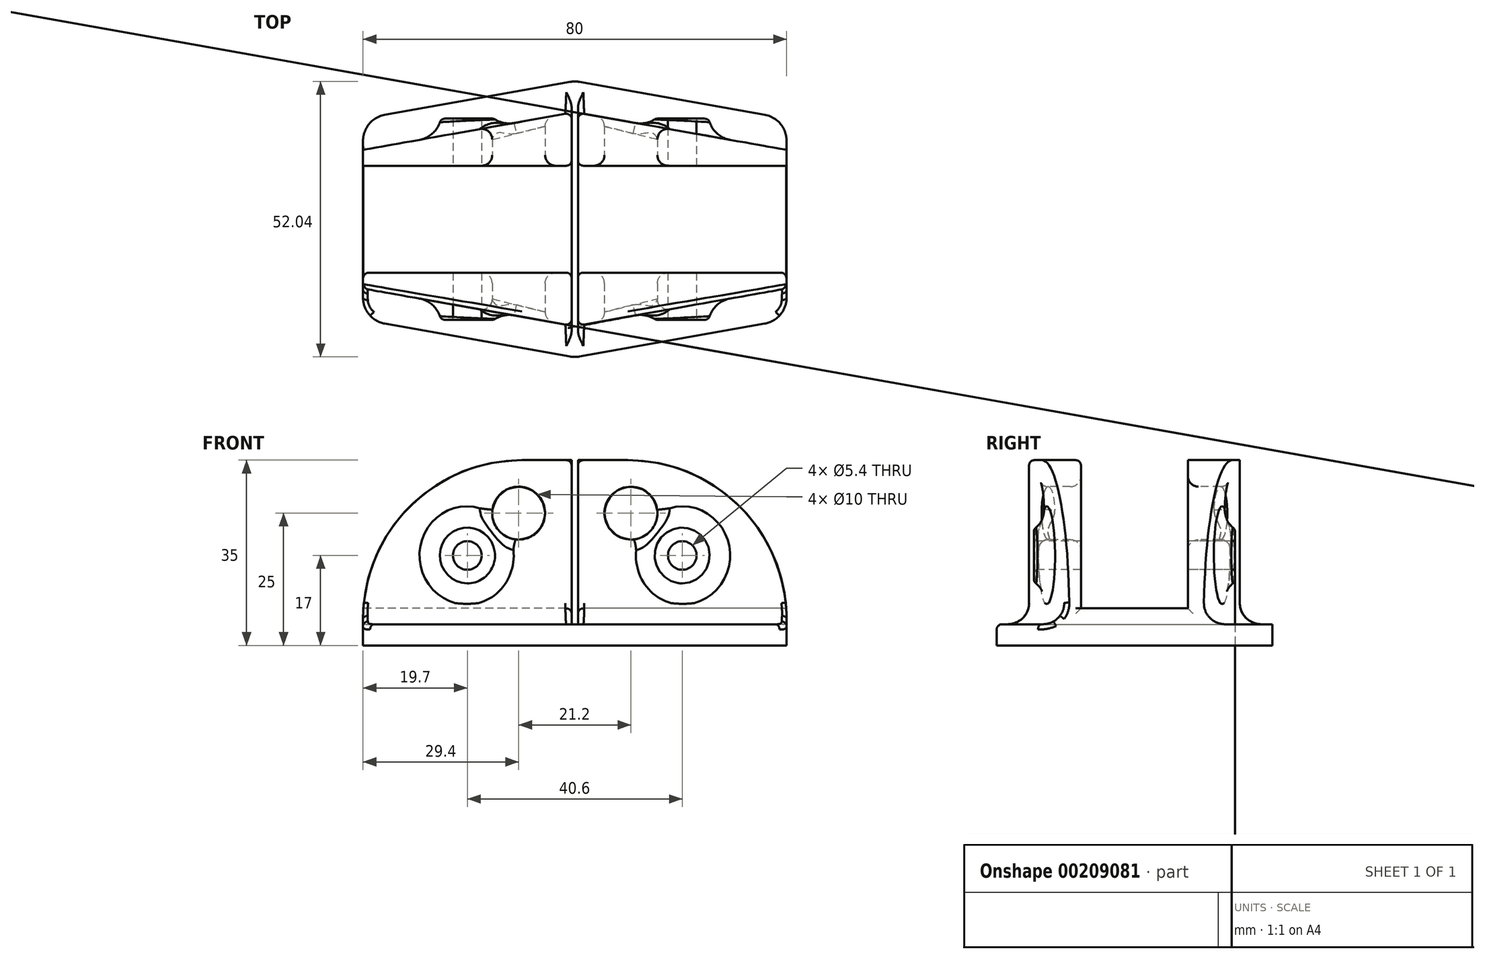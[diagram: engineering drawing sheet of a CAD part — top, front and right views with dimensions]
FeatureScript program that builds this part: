
annotation { "Feature Type Name" : "Feature", "Feature Type Description" : "" }
export const myFeature = defineFeature(function(context is Context, id is Id, definition is map)
    precondition{}
    {
        {
            var Q0;
            Q0=qCreatedBy(makeId("Top.planeOp"),FACE);
            var sketch = newSketch(context, id + "F0", { "sketchPlane" : qUnion([Q0])});
            skLineSegment(sketch, "E0.rect.bottom", {"start": v(40, 10.1) * mm, "end": v(-40, 10.1) * mm});
            skLineSegment(sketch, "E0.rect.top", {"start": v(40, -10.1) * mm, "end": v(-40, -10.1) * mm});
            skLineSegment(sketch, "E0.rect.left", {"start": v(40, 10.1) * mm, "end": v(40, -10.1) * mm});
            skLineSegment(sketch, "E0.rect.right", {"start": v(-40, 10.1) * mm, "end": v(-40, -10.1) * mm});
            skPoint(sketch, "E0.rect.middle", {"position": v(0, 0) * mm});
            skLineSegment(sketch, "E1", {"start": v(-40, 20.1) * mm, "end": v(40, 20.1) * mm, "construction": true});
            skLineSegment(sketch, "E2", {"start": v(40, -20.1) * mm, "end": v(-40, -20.1) * mm, "construction": true});
            skLineSegment(sketch, "E3", {"start": v(40, 10.1) * mm, "end": v(40, 20.1) * mm});
            skLineSegment(sketch, "E4", {"start": v(40, -10.1) * mm, "end": v(40, -20.1) * mm});
            skLineSegment(sketch, "E5.rect.bottom", {"start": v(0.6, 20.1) * mm, "end": v(-0.6, 20.1) * mm});
            skLineSegment(sketch, "E5.rect.top", {"start": v(0.6, -20.1) * mm, "end": v(-0.6, -20.1) * mm});
            skLineSegment(sketch, "E5.rect.left", {"start": v(0.6, 20.1) * mm, "end": v(0.6, 10.1) * mm});
            skLineSegment(sketch, "E5.rect.right", {"start": v(-0.6, 20.1) * mm, "end": v(-0.6, 10.1) * mm});
            skLineSegment(sketch, "E6", {"start": v(-40, -10.1) * mm, "end": v(-40, -20.1) * mm});
            skLineSegment(sketch, "E7", {"start": v(-40, 10.1) * mm, "end": v(-40, 20.1) * mm});
            skLineSegment(sketch, "E8.trimOffspring", {"start": v(0.6, -10.1) * mm, "end": v(0.6, -20.1) * mm});
            skLineSegment(sketch, "E9.trimOffspring", {"start": v(-0.6, -10.1) * mm, "end": v(-0.6, -20.1) * mm});
            skLineSegment(sketch, "E10", {"start": v(-40, 26.1) * mm, "end": v(40, 26.1) * mm, "construction": true});
            skLineSegment(sketch, "E11", {"start": v(40, -26.1) * mm, "end": v(-40, -26.1) * mm, "construction": true});
            skLineSegment(sketch, "E12", {"start": v(40, -20.1) * mm, "end": v(40, -26.1) * mm});
            skLineSegment(sketch, "E13", {"start": v(-40, -26.1) * mm, "end": v(-40, -20.1) * mm});
            skLineSegment(sketch, "E14", {"start": v(-40, 20.1) * mm, "end": v(-40, 26.1) * mm});
            skLineSegment(sketch, "E15", {"start": v(40, 26.1) * mm, "end": v(40, 20.1) * mm});
            skLineSegment(sketch, "E16", {"start": v(0.6, 10.1) * mm, "end": v(0.6, -10.1) * mm});
            skLineSegment(sketch, "E17", {"start": v(-0.6, -10.1) * mm, "end": v(-0.6, 10.1) * mm});
            skLineSegment(sketch, "E18", {"start": v(0.6, 20.1) * mm, "end": v(40, 13.1) * mm});
            skLineSegment(sketch, "E19", {"start": v(-0.6, 20.1) * mm, "end": v(-40, 13.1) * mm});
            skLineSegment(sketch, "E20", {"start": v(40, -13.1) * mm, "end": v(0.6, -20.1) * mm});
            skLineSegment(sketch, "E21", {"start": v(-0.6, -20.1) * mm, "end": v(-40, -13.1) * mm});
            skLineSegment(sketch, "E22", {"start": v(0, 26.1) * mm, "end": v(40, 19) * mm});
            skLineSegment(sketch, "E23", {"start": v(0, 26.1) * mm, "end": v(-40, 19) * mm});
            skLineSegment(sketch, "E24", {"start": v(0, -26.1) * mm, "end": v(40, -19) * mm});
            skLineSegment(sketch, "E25", {"start": v(0, -26.1) * mm, "end": v(-40, -19) * mm});
            skSolve(sketch);
        }
        {
            var Q0;
            Q0=makeQuery(id+"F0.imprint","IMPRINT",FACE,{"disambiguationData":[TD([[makeQuery(id+"F0.imprint","IMPRINT",EDGE,{"derivedFrom":sQuery(id+"F0.wireOp",EDGE,"E5.rect.bottom")}),-1.0]])]});
            var Q1;
            {var subQ4=sQuery(id+"F0.wireOp",EDGE,"E5.rect.right");Q1=makeQuery(id+"F0.imprint","IMPRINT",FACE,{"disambiguationData":[TD([[makeQuery(id+"F0.imprint","IMPRINT",EDGE,{"derivedFrom":subQ4}),-1.0]])]});}
            var Q2;
            Q2=makeQuery(id+"F0.imprint","IMPRINT",FACE,{"disambiguationData":[TD([[makeQuery(id+"F0.imprint","IMPRINT",EDGE,{"derivedFrom":sQuery(id+"F0.wireOp",EDGE,"E5.rect.bottom")}),1.0]])]});
            var Q3;
            {var subQ1=sQuery(id+"F0.wireOp",EDGE,"E5.rect.left");Q3=makeQuery(id+"F0.imprint","IMPRINT",FACE,{"disambiguationData":[TD([[makeQuery(id+"F0.imprint","IMPRINT",EDGE,{"derivedFrom":subQ1}),1.0]])]});}
            var Q4;
            {var subQ1=sQuery(id+"F0.wireOp",EDGE,"E0.rect.left");Q4=makeQuery(id+"F0.imprint","IMPRINT",FACE,{"disambiguationData":[TD([[makeQuery(id+"F0.imprint","IMPRINT",EDGE,{"derivedFrom":subQ1}),-1.0]])]});}
            var Q5;
            Q5=makeQuery(id+"F0.imprint","IMPRINT",FACE,{"disambiguationData":[TD([[makeQuery(id+"F0.imprint","IMPRINT",EDGE,{"derivedFrom":sQuery(id+"F0.wireOp",EDGE,"E5.rect.top")}),-1.0]])]});
            var Q6;
            {var subQ1=sQuery(id+"F0.wireOp",EDGE,"E9.trimOffspring");Q6=makeQuery(id+"F0.imprint","IMPRINT",FACE,{"disambiguationData":[TD([[makeQuery(id+"F0.imprint","IMPRINT",EDGE,{"derivedFrom":subQ1}),-1.0]])]});}
            var Q7;
            {var subQ1=sQuery(id+"F0.wireOp",EDGE,"E8.trimOffspring");Q7=makeQuery(id+"F0.imprint","IMPRINT",FACE,{"disambiguationData":[TD([[makeQuery(id+"F0.imprint","IMPRINT",EDGE,{"derivedFrom":subQ1}),1.0]])]});}
            var Q8;
            Q8=makeQuery(id+"F0.imprint","IMPRINT",FACE,{"disambiguationData":[TD([[makeQuery(id+"F0.imprint","IMPRINT",EDGE,{"derivedFrom":sQuery(id+"F0.wireOp",EDGE,"E5.rect.top")}),1.0]])]});
            var Q9;
            {var subQ1=sQuery(id+"F0.wireOp",EDGE,"E16");Q9=makeQuery(id+"F0.imprint","IMPRINT",FACE,{"disambiguationData":[TD([[makeQuery(id+"F0.imprint","IMPRINT",EDGE,{"derivedFrom":subQ1}),-1.0]])]});}
            var Q10;
            {var subQ1=sQuery(id+"F0.wireOp",EDGE,"E0.rect.right");Q10=makeQuery(id+"F0.imprint","IMPRINT",FACE,{"disambiguationData":[TD([[makeQuery(id+"F0.imprint","IMPRINT",EDGE,{"derivedFrom":subQ1}),1.0]])]});}
            extrude(context, id + "F1", {"entities" : qUnion([Q0, Q1, Q2, Q3, Q4, Q5, Q6, Q7, Q8, Q9, Q10]), "depth" : 4 * mm});
        }
        {
            var Q0;
            {var subQ1=sQuery(id+"F0.wireOp",EDGE,"E9.trimOffspring");Q0=makeQuery(id+"F0.imprint","IMPRINT",FACE,{"disambiguationData":[TD([[makeQuery(id+"F0.imprint","IMPRINT",EDGE,{"derivedFrom":subQ1}),-1.0]])]});}
            var Q1;
            {var subQ1=sQuery(id+"F0.wireOp",EDGE,"E8.trimOffspring");Q1=makeQuery(id+"F0.imprint","IMPRINT",FACE,{"disambiguationData":[TD([[makeQuery(id+"F0.imprint","IMPRINT",EDGE,{"derivedFrom":subQ1}),1.0]])]});}
            var Q2;
            {var subQ1=sQuery(id+"F0.wireOp",EDGE,"E5.rect.left");Q2=makeQuery(id+"F0.imprint","IMPRINT",FACE,{"disambiguationData":[TD([[makeQuery(id+"F0.imprint","IMPRINT",EDGE,{"derivedFrom":subQ1}),1.0]])]});}
            var Q3;
            {var subQ4=sQuery(id+"F0.wireOp",EDGE,"E5.rect.right");Q3=makeQuery(id+"F0.imprint","IMPRINT",FACE,{"disambiguationData":[TD([[makeQuery(id+"F0.imprint","IMPRINT",EDGE,{"derivedFrom":subQ4}),-1.0]])]});}
            extrude(context, id + "F2", {"entities" : qUnion([Q0, Q1, Q2, Q3]), "operationType" : NewBodyOperationType.ADD, "depth" : 35 * mm});
        }
        {
            var Q0;
            {var subQ1=sQuery(id+"F0.wireOp",EDGE,"E0.rect.right");Q0=makeQuery(id+"F0.imprint","IMPRINT",FACE,{"disambiguationData":[TD([[makeQuery(id+"F0.imprint","IMPRINT",EDGE,{"derivedFrom":subQ1}),1.0]])]});}
            var Q1;
            {var subQ1=sQuery(id+"F0.wireOp",EDGE,"E0.rect.left");Q1=makeQuery(id+"F0.imprint","IMPRINT",FACE,{"disambiguationData":[TD([[makeQuery(id+"F0.imprint","IMPRINT",EDGE,{"derivedFrom":subQ1}),-1.0]])]});}
            extrude(context, id + "F3", {"entities" : qUnion([Q0, Q1]), "operationType" : NewBodyOperationType.ADD, "depth" : 7 * mm});
        }
        {
            var Q0;
            Q0=qCreatedBy(makeId("Front.planeOp"),FACE);
            var sketch = newSketch(context, id + "F4", { "sketchPlane" : qUnion([Q0])});
            skLineSegment(sketch, "E26.0", {"start": v(-0.6, 7) * mm, "end": v(-40, 7) * mm});
            skLineSegment(sketch, "E27.0", {"start": v(40, 7) * mm, "end": v(0.6, 7) * mm});
            skLineSegment(sketch, "E28", {"start": v(-20.3, 7) * mm, "end": v(-20.3, 17) * mm, "construction": true});
            skLineSegment(sketch, "E29", {"start": v(20.3, 7) * mm, "end": v(20.3, 17) * mm, "construction": true});
            skCircle(sketch, "E30", {"center": v(-20.3, 17) * mm, "radius": 2.7 * mm});
            skCircle(sketch, "E31", {"center": v(20.3, 17) * mm, "radius": 2.7 * mm});
            skCircle(sketch, "E32", {"center": v(-20.3, 17) * mm, "radius": 5 * mm});
            skCircle(sketch, "E33", {"center": v(20.3, 17) * mm, "radius": 5 * mm});
            skCircle(sketch, "E34", {"center": v(-10.6, 25) * mm, "radius": 5 * mm});
            skCircle(sketch, "E35", {"center": v(10.6, 25) * mm, "radius": 5 * mm});
            skLineSegment(sketch, "E36.0", {"start": v(-0.6, 35) * mm, "end": v(-0.6, 7) * mm});
            skLineSegment(sketch, "E37.0", {"start": v(0.6, 35) * mm, "end": v(0.6, 7) * mm});
            skLineSegment(sketch, "E38", {"start": v(-10.6, 25) * mm, "end": v(-0.6, 25) * mm, "construction": true});
            skLineSegment(sketch, "E39", {"start": v(10.6, 25) * mm, "end": v(0.6, 25) * mm, "construction": true});
            skSolve(sketch);
        }
        {
            var Q0;
            Q0=makeQuery(id+"F4.imprint","IMPRINT",FACE,{"disambiguationData":[TD([[makeQuery(id+"F4.imprint","IMPRINT",EDGE,{"derivedFrom":sQuery(id+"F4.wireOp",EDGE,"E30")}),1.0]])]});
            var Q1;
            Q1=makeQuery(id+"F4.imprint","IMPRINT",FACE,{"disambiguationData":[TD([[makeQuery(id+"F4.imprint","IMPRINT",EDGE,{"derivedFrom":sQuery(id+"F4.wireOp",EDGE,"E31")}),1.0]])]});
            extrude(context, id + "F5", {"entities" : qUnion([Q0, Q1]), "operationType" : NewBodyOperationType.REMOVE, "endBound" : BoundingType.SYMMETRIC, "oppositeDirection" : true, "depth" : 50 * mm});
        }
        {
            var Q0;
            Q0=makeQuery(id+"F4.imprint","IMPRINT",FACE,{"disambiguationData":[TD([[makeQuery(id+"F4.imprint","IMPRINT",EDGE,{"derivedFrom":sQuery(id+"F4.wireOp",EDGE,"E30")}),-1.0]])]});
            var Q1;
            Q1=makeQuery(id+"F4.imprint","IMPRINT",FACE,{"disambiguationData":[TD([[makeQuery(id+"F4.imprint","IMPRINT",EDGE,{"derivedFrom":sQuery(id+"F4.wireOp",EDGE,"E31")}),-1.0]])]});
            extrude(context, id + "F6", {"entities" : qUnion([Q0, Q1]), "operationType" : NewBodyOperationType.ADD, "endBound" : BoundingType.SYMMETRIC, "depth" : 38 * mm});
        }
        {
            var Q0;
            Q0=makeQuery(id+"F4.imprint","IMPRINT",FACE,{"disambiguationData":[TD([[makeQuery(id+"F4.imprint","IMPRINT",EDGE,{"derivedFrom":sQuery(id+"F4.wireOp",EDGE,"E30")}),-1.0]])]});
            var Q1;
            Q1=makeQuery(id+"F4.imprint","IMPRINT",FACE,{"disambiguationData":[TD([[makeQuery(id+"F4.imprint","IMPRINT",EDGE,{"derivedFrom":sQuery(id+"F4.wireOp",EDGE,"E31")}),-1.0]])]});
            extrude(context, id + "F7", {"entities" : qUnion([Q0, Q1]), "operationType" : NewBodyOperationType.REMOVE, "endBound" : BoundingType.SYMMETRIC, "oppositeDirection" : true, "depth" : 20.2 * mm});
        }
        {
            var Q0;
            Q0=makeQuery(id+"F4.imprint","IMPRINT",FACE,{"disambiguationData":[TD([[makeQuery(id+"F4.imprint","IMPRINT",EDGE,{"derivedFrom":sQuery(id+"F4.wireOp",EDGE,"E34")}),1.0]])]});
            var Q1;
            Q1=makeQuery(id+"F4.imprint","IMPRINT",FACE,{"disambiguationData":[TD([[makeQuery(id+"F4.imprint","IMPRINT",EDGE,{"derivedFrom":sQuery(id+"F4.wireOp",EDGE,"E35")}),1.0]])]});
            extrude(context, id + "F8", {"entities" : qUnion([Q0, Q1]), "operationType" : NewBodyOperationType.REMOVE, "endBound" : BoundingType.SYMMETRIC, "oppositeDirection" : true, "depth" : 50 * mm});
        }
        {
            var Q0;
            Q0=makeQuery(id+"F2.opExtrude","CAP_EDGE",EDGE,{"disambiguationData":[OSD([sQuery(id+"F0.wireOp",EDGE,"E4")])],"isStart":false});
            var Q1;
            Q1=makeQuery(id+"F2.opExtrude","CAP_EDGE",EDGE,{"disambiguationData":[OSD([sQuery(id+"F0.wireOp",EDGE,"E6")])],"isStart":false});
            var Q2;
            Q2=makeQuery(id+"F2.opExtrude","CAP_EDGE",EDGE,{"disambiguationData":[OSD([sQuery(id+"F0.wireOp",EDGE,"E7")])],"isStart":false});
            var Q3;
            Q3=makeQuery(id+"F2.opExtrude","CAP_EDGE",EDGE,{"disambiguationData":[OSD([sQuery(id+"F0.wireOp",EDGE,"E3")])],"isStart":false});
            fillet(context, id + "F9", {"entities" : qUnion([Q0, Q1, Q2, Q3]), "radius" : 30 * mm, "tangentPropagation" : true, "allowEdgeOverflow" : false});
        }
        {
            var Q0;
            Q0=makeQuery(id+"F1.opExtrude","SWEPT_EDGE",EDGE,{"disambiguationData":[OSD([sQuery(id+"F0.wireOp",EDGE,"E7"),sQuery(id+"F0.wireOp",EDGE,"E23")])]});
            var Q1;
            Q1=makeQuery(id+"F1.opExtrude","SWEPT_EDGE",EDGE,{"disambiguationData":[OSD([sQuery(id+"F0.wireOp",EDGE,"E6"),sQuery(id+"F0.wireOp",EDGE,"E25")])]});
            var Q2;
            Q2=makeQuery(id+"F1.opExtrude","SWEPT_EDGE",EDGE,{"disambiguationData":[OSD([sQuery(id+"F0.wireOp",EDGE,"E22"),sQuery(id+"F0.wireOp",EDGE,"E23")])]});
            var Q3;
            Q3=makeQuery(id+"F1.opExtrude","SWEPT_EDGE",EDGE,{"disambiguationData":[OSD([sQuery(id+"F0.wireOp",EDGE,"E3"),sQuery(id+"F0.wireOp",EDGE,"E22")])]});
            var Q4;
            Q4=makeQuery(id+"F1.opExtrude","SWEPT_EDGE",EDGE,{"disambiguationData":[OSD([sQuery(id+"F0.wireOp",EDGE,"E4"),sQuery(id+"F0.wireOp",EDGE,"E24")])]});
            var Q5;
            Q5=makeQuery(id+"F1.opExtrude","SWEPT_EDGE",EDGE,{"disambiguationData":[OSD([sQuery(id+"F0.wireOp",EDGE,"E24"),sQuery(id+"F0.wireOp",EDGE,"E25")])]});
            fillet(context, id + "F10", {"entities" : qUnion([Q0, Q1, Q2, Q3, Q4, Q5]), "radius" : 5 * mm, "tangentPropagation" : true, "allowEdgeOverflow" : false});
        }
        {
            var Q0;
            Q0=makeQuery(id+"F2.boolean.opBoolean","INTERSECT",EDGE,{"derivedFrom":[makeQuery(id+"F1.opExtrude","CAP_FACE",FACE,{"disambiguationData":[OSD([sQuery(id+"F0.wireOp",EDGE,"E0.rect.left"),sQuery(id+"F0.wireOp",EDGE,"E0.rect.right"),sQuery(id+"F0.wireOp",EDGE,"E3"),sQuery(id+"F0.wireOp",EDGE,"E4"),sQuery(id+"F0.wireOp",EDGE,"E6"),sQuery(id+"F0.wireOp",EDGE,"E7"),sQuery(id+"F0.wireOp",EDGE,"E22"),sQuery(id+"F0.wireOp",EDGE,"E23"),sQuery(id+"F0.wireOp",EDGE,"E24"),sQuery(id+"F0.wireOp",EDGE,"E25")])],"isStart":false}),makeQuery(id+"F2.opExtrude","SWEPT_FACE",FACE,{"disambiguationData":[OSD([sQuery(id+"F0.wireOp",EDGE,"E21")])]})]});
            var Q1;
            Q1=makeQuery(id+"F2.boolean.opBoolean","INTERSECT",EDGE,{"derivedFrom":[makeQuery(id+"F1.opExtrude","CAP_FACE",FACE,{"disambiguationData":[OSD([sQuery(id+"F0.wireOp",EDGE,"E0.rect.left"),sQuery(id+"F0.wireOp",EDGE,"E0.rect.right"),sQuery(id+"F0.wireOp",EDGE,"E3"),sQuery(id+"F0.wireOp",EDGE,"E4"),sQuery(id+"F0.wireOp",EDGE,"E6"),sQuery(id+"F0.wireOp",EDGE,"E7"),sQuery(id+"F0.wireOp",EDGE,"E22"),sQuery(id+"F0.wireOp",EDGE,"E23"),sQuery(id+"F0.wireOp",EDGE,"E24"),sQuery(id+"F0.wireOp",EDGE,"E25")])],"isStart":false}),makeQuery(id+"F2.opExtrude","SWEPT_FACE",FACE,{"disambiguationData":[OSD([sQuery(id+"F0.wireOp",EDGE,"E20")])]})]});
            var Q2;
            Q2=makeQuery(id+"F2.boolean.opBoolean","INTERSECT",EDGE,{"derivedFrom":[makeQuery(id+"F1.opExtrude","CAP_FACE",FACE,{"disambiguationData":[OSD([sQuery(id+"F0.wireOp",EDGE,"E0.rect.left"),sQuery(id+"F0.wireOp",EDGE,"E0.rect.right"),sQuery(id+"F0.wireOp",EDGE,"E3"),sQuery(id+"F0.wireOp",EDGE,"E4"),sQuery(id+"F0.wireOp",EDGE,"E6"),sQuery(id+"F0.wireOp",EDGE,"E7"),sQuery(id+"F0.wireOp",EDGE,"E22"),sQuery(id+"F0.wireOp",EDGE,"E23"),sQuery(id+"F0.wireOp",EDGE,"E24"),sQuery(id+"F0.wireOp",EDGE,"E25")])],"isStart":false}),makeQuery(id+"F2.opExtrude","SWEPT_FACE",FACE,{"disambiguationData":[OSD([sQuery(id+"F0.wireOp",EDGE,"E19")])]})]});
            var Q3;
            Q3=makeQuery(id+"F2.boolean.opBoolean","INTERSECT",EDGE,{"derivedFrom":[makeQuery(id+"F1.opExtrude","CAP_FACE",FACE,{"disambiguationData":[OSD([sQuery(id+"F0.wireOp",EDGE,"E0.rect.left"),sQuery(id+"F0.wireOp",EDGE,"E0.rect.right"),sQuery(id+"F0.wireOp",EDGE,"E3"),sQuery(id+"F0.wireOp",EDGE,"E4"),sQuery(id+"F0.wireOp",EDGE,"E6"),sQuery(id+"F0.wireOp",EDGE,"E7"),sQuery(id+"F0.wireOp",EDGE,"E22"),sQuery(id+"F0.wireOp",EDGE,"E23"),sQuery(id+"F0.wireOp",EDGE,"E24"),sQuery(id+"F0.wireOp",EDGE,"E25")])],"isStart":false}),makeQuery(id+"F2.opExtrude","SWEPT_FACE",FACE,{"disambiguationData":[OSD([sQuery(id+"F0.wireOp",EDGE,"E18")])]})]});
            fillet(context, id + "F11", {"entities" : qUnion([Q0, Q1, Q2, Q3]), "radius" : 4 * mm, "tangentPropagation" : true, "allowEdgeOverflow" : false});
        }
        {
            var Q0;
            Q0=makeQuery(id+"F11.opFillet","BLEND_EDGE",EDGE,{"blendedFrom":[makeQuery(id+"F2.boolean.opBoolean","INTERSECT",EDGE,{"derivedFrom":[makeQuery(id+"F1.opExtrude","CAP_FACE",FACE,{"disambiguationData":[OSD([sQuery(id+"F0.wireOp",EDGE,"E0.rect.left"),sQuery(id+"F0.wireOp",EDGE,"E0.rect.right"),sQuery(id+"F0.wireOp",EDGE,"E3"),sQuery(id+"F0.wireOp",EDGE,"E4"),sQuery(id+"F0.wireOp",EDGE,"E6"),sQuery(id+"F0.wireOp",EDGE,"E7"),sQuery(id+"F0.wireOp",EDGE,"E22"),sQuery(id+"F0.wireOp",EDGE,"E23"),sQuery(id+"F0.wireOp",EDGE,"E24"),sQuery(id+"F0.wireOp",EDGE,"E25")])],"isStart":false}),makeQuery(id+"F2.opExtrude","SWEPT_FACE",FACE,{"disambiguationData":[OSD([sQuery(id+"F0.wireOp",EDGE,"E18")])]})]}),makeQuery(id+"F3.boolean.opBoolean","MERGE",FACE,{"derivedFrom":[makeQuery(id+"F2.opExtrude","SWEPT_FACE",FACE,{"disambiguationData":[OSD([sQuery(id+"F0.wireOp",EDGE,"E5.rect.left")])]}),makeQuery(id+"F2.opExtrude","SWEPT_FACE",FACE,{"disambiguationData":[OSD([sQuery(id+"F0.wireOp",EDGE,"E8.trimOffspring")])]}),makeQuery(id+"F3.opExtrude","SWEPT_FACE",FACE,{"disambiguationData":[OSD([sQuery(id+"F0.wireOp",EDGE,"E16")])]})]})],"blendedInto":[makeQuery(id+"F3.boolean.opBoolean","MERGE",FACE,{"derivedFrom":[makeQuery(id+"F2.opExtrude","SWEPT_FACE",FACE,{"disambiguationData":[OSD([sQuery(id+"F0.wireOp",EDGE,"E5.rect.left")])]}),makeQuery(id+"F2.opExtrude","SWEPT_FACE",FACE,{"disambiguationData":[OSD([sQuery(id+"F0.wireOp",EDGE,"E8.trimOffspring")])]}),makeQuery(id+"F3.opExtrude","SWEPT_FACE",FACE,{"disambiguationData":[OSD([sQuery(id+"F0.wireOp",EDGE,"E16")])]})]})]});
            var Q1;
            Q1=makeQuery(id+"F11.opFillet","BLEND_EDGE",EDGE,{"blendedFrom":[makeQuery(id+"F2.boolean.opBoolean","INTERSECT",EDGE,{"derivedFrom":[makeQuery(id+"F1.opExtrude","CAP_FACE",FACE,{"disambiguationData":[OSD([sQuery(id+"F0.wireOp",EDGE,"E0.rect.left"),sQuery(id+"F0.wireOp",EDGE,"E0.rect.right"),sQuery(id+"F0.wireOp",EDGE,"E3"),sQuery(id+"F0.wireOp",EDGE,"E4"),sQuery(id+"F0.wireOp",EDGE,"E6"),sQuery(id+"F0.wireOp",EDGE,"E7"),sQuery(id+"F0.wireOp",EDGE,"E22"),sQuery(id+"F0.wireOp",EDGE,"E23"),sQuery(id+"F0.wireOp",EDGE,"E24"),sQuery(id+"F0.wireOp",EDGE,"E25")])],"isStart":false}),makeQuery(id+"F2.opExtrude","SWEPT_FACE",FACE,{"disambiguationData":[OSD([sQuery(id+"F0.wireOp",EDGE,"E19")])]})]}),makeQuery(id+"F3.boolean.opBoolean","MERGE",FACE,{"derivedFrom":[makeQuery(id+"F2.opExtrude","SWEPT_FACE",FACE,{"disambiguationData":[OSD([sQuery(id+"F0.wireOp",EDGE,"E5.rect.right")])]}),makeQuery(id+"F2.opExtrude","SWEPT_FACE",FACE,{"disambiguationData":[OSD([sQuery(id+"F0.wireOp",EDGE,"E9.trimOffspring")])]}),makeQuery(id+"F3.opExtrude","SWEPT_FACE",FACE,{"disambiguationData":[OSD([sQuery(id+"F0.wireOp",EDGE,"E17")])]})]})],"blendedInto":[makeQuery(id+"F3.boolean.opBoolean","MERGE",FACE,{"derivedFrom":[makeQuery(id+"F2.opExtrude","SWEPT_FACE",FACE,{"disambiguationData":[OSD([sQuery(id+"F0.wireOp",EDGE,"E5.rect.right")])]}),makeQuery(id+"F2.opExtrude","SWEPT_FACE",FACE,{"disambiguationData":[OSD([sQuery(id+"F0.wireOp",EDGE,"E9.trimOffspring")])]}),makeQuery(id+"F3.opExtrude","SWEPT_FACE",FACE,{"disambiguationData":[OSD([sQuery(id+"F0.wireOp",EDGE,"E17")])]})]})]});
            var Q2;
            Q2=makeQuery(id+"F2.opExtrude","SWEPT_EDGE",EDGE,{"disambiguationData":[OSD([sQuery(id+"F0.wireOp",EDGE,"E0.rect.bottom"),sQuery(id+"F0.wireOp",EDGE,"E5.rect.right"),sQuery(id+"F0.wireOp",EDGE,"E17")])]});
            var Q3;
            Q3=makeQuery(id+"F2.opExtrude","SWEPT_EDGE",EDGE,{"disambiguationData":[OSD([sQuery(id+"F0.wireOp",EDGE,"E0.rect.bottom"),sQuery(id+"F0.wireOp",EDGE,"E5.rect.left"),sQuery(id+"F0.wireOp",EDGE,"E16")])]});
            var Q4;
            Q4=makeQuery(id+"F2.opExtrude","SWEPT_EDGE",EDGE,{"disambiguationData":[OSD([sQuery(id+"F0.wireOp",EDGE,"E5.rect.top"),sQuery(id+"F0.wireOp",EDGE,"E8.trimOffspring"),sQuery(id+"F0.wireOp",EDGE,"E20")])]});
            var Q5;
            Q5=makeQuery(id+"F2.opExtrude","SWEPT_EDGE",EDGE,{"disambiguationData":[OSD([sQuery(id+"F0.wireOp",EDGE,"E5.rect.top"),sQuery(id+"F0.wireOp",EDGE,"E9.trimOffspring"),sQuery(id+"F0.wireOp",EDGE,"E21")])]});
            var Q6;
            Q6=makeQuery(id+"F2.opExtrude","SWEPT_EDGE",EDGE,{"disambiguationData":[OSD([sQuery(id+"F0.wireOp",EDGE,"E0.rect.top"),sQuery(id+"F0.wireOp",EDGE,"E9.trimOffspring"),sQuery(id+"F0.wireOp",EDGE,"E17")])]});
            var Q7;
            Q7=makeQuery(id+"F2.opExtrude","SWEPT_EDGE",EDGE,{"disambiguationData":[OSD([sQuery(id+"F0.wireOp",EDGE,"E0.rect.top"),sQuery(id+"F0.wireOp",EDGE,"E8.trimOffspring"),sQuery(id+"F0.wireOp",EDGE,"E16")])]});
            var Q8;
            Q8=makeQuery(id+"F3.opExtrude","CAP_EDGE",EDGE,{"disambiguationData":[OSD([sQuery(id+"F0.wireOp",EDGE,"E17")])],"isStart":false});
            var Q9;
            Q9=makeQuery(id+"F3.opExtrude","CAP_EDGE",EDGE,{"disambiguationData":[OSD([sQuery(id+"F0.wireOp",EDGE,"E16")])],"isStart":false});
            var Q10;
            {var subQ0=sQuery(id+"F0.wireOp",EDGE,"E0.rect.top");Q10=makeQuery(id+"F3.opExtrude","CAP_EDGE",EDGE,{"disambiguationData":[OSD([subQ0]),TDD([makeQuery(id+"F0.imprint","IMPRINT",EDGE,{"disambiguationData":[TD([[makeQuery(id+"F0.imprint","INTERSECT",VERTEX,{"derivedFrom":[subQ0,sQuery(id+"F0.wireOp",EDGE,"E0.rect.left"),sQuery(id+"F0.wireOp",EDGE,"E4")]}),-1.0]])],"derivedFrom":subQ0})])],"isStart":false});}
            var Q11;
            {var subQ0=sQuery(id+"F0.wireOp",EDGE,"E0.rect.bottom");Q11=makeQuery(id+"F3.opExtrude","CAP_EDGE",EDGE,{"disambiguationData":[OSD([subQ0]),TDD([makeQuery(id+"F0.imprint","IMPRINT",EDGE,{"disambiguationData":[TD([[makeQuery(id+"F0.imprint","INTERSECT",VERTEX,{"derivedFrom":[subQ0,sQuery(id+"F0.wireOp",EDGE,"E0.rect.left"),sQuery(id+"F0.wireOp",EDGE,"E3")]}),-1.0]])],"derivedFrom":subQ0})])],"isStart":false});}
            var Q12;
            {var subQ0=sQuery(id+"F0.wireOp",EDGE,"E0.rect.bottom");Q12=makeQuery(id+"F3.opExtrude","CAP_EDGE",EDGE,{"disambiguationData":[OSD([subQ0]),TDD([makeQuery(id+"F0.imprint","IMPRINT",EDGE,{"disambiguationData":[TD([[makeQuery(id+"F0.imprint","INTERSECT",VERTEX,{"derivedFrom":[subQ0,sQuery(id+"F0.wireOp",EDGE,"E0.rect.right"),sQuery(id+"F0.wireOp",EDGE,"E7")]}),1.0]])],"derivedFrom":subQ0})])],"isStart":false});}
            var Q13;
            {var subQ0=sQuery(id+"F0.wireOp",EDGE,"E0.rect.top");Q13=makeQuery(id+"F3.opExtrude","CAP_EDGE",EDGE,{"disambiguationData":[OSD([subQ0]),TDD([makeQuery(id+"F0.imprint","IMPRINT",EDGE,{"disambiguationData":[TD([[makeQuery(id+"F0.imprint","INTERSECT",VERTEX,{"derivedFrom":[subQ0,sQuery(id+"F0.wireOp",EDGE,"E0.rect.right"),sQuery(id+"F0.wireOp",EDGE,"E6")]}),1.0]])],"derivedFrom":subQ0})])],"isStart":false});}
            var Q14;
            Q14=makeQuery(id+"F3.opExtrude","CAP_EDGE",EDGE,{"disambiguationData":[OSD([sQuery(id+"F0.wireOp",EDGE,"E0.rect.right")])],"isStart":false});
            var Q15;
            Q15=makeQuery(id+"F3.opExtrude","CAP_EDGE",EDGE,{"disambiguationData":[OSD([sQuery(id+"F0.wireOp",EDGE,"E0.rect.left")])],"isStart":false});
            fillet(context, id + "F12", {"entities" : qUnion([Q0, Q1, Q2, Q3, Q4, Q5, Q6, Q7, Q8, Q9, Q10, Q11, Q12, Q13, Q14, Q15]), "radius" : 1 * mm, "tangentPropagation" : true, "allowEdgeOverflow" : false});
        }
        {
            var Q0;
            Q0=makeQuery(id+"F9.opFillet","BLEND_EDGE",EDGE,{"blendedFrom":[makeQuery(id+"F2.opExtrude","CAP_EDGE",EDGE,{"disambiguationData":[OSD([sQuery(id+"F0.wireOp",EDGE,"E4")])],"isStart":false}),makeQuery(id+"F2.opExtrude","SWEPT_FACE",FACE,{"disambiguationData":[OSD([sQuery(id+"F0.wireOp",EDGE,"E20")])]})],"blendedInto":[makeQuery(id+"F2.opExtrude","SWEPT_FACE",FACE,{"disambiguationData":[OSD([sQuery(id+"F0.wireOp",EDGE,"E20")])]})]});
            var Q1;
            {var subQ0=sQuery(id+"F0.wireOp",EDGE,"E3");var subQ1=sQuery(id+"F0.wireOp",EDGE,"E18");Q1=makeQuery(id+"F9.opFillet","BLEND_EDGE",EDGE,{"blendedFrom":[makeQuery(id+"F2.opExtrude","CAP_EDGE",EDGE,{"disambiguationData":[OSD([subQ0])],"isStart":false}),makeQuery(id+"F6.boolean.opBoolean","SPLIT",FACE,{"disambiguationData":[TD([makeQuery(id+"F2.opExtrude","SWEPT_FACE",FACE,{"disambiguationData":[OSD([subQ0])]})])],"derivedFrom":makeQuery(id+"F2.opExtrude","SWEPT_FACE",FACE,{"disambiguationData":[OSD([subQ1])]})})],"blendedInto":[makeQuery(id+"F6.boolean.opBoolean","SPLIT",FACE,{"disambiguationData":[TD([makeQuery(id+"F2.opExtrude","SWEPT_FACE",FACE,{"disambiguationData":[OSD([subQ0])]})])],"derivedFrom":makeQuery(id+"F2.opExtrude","SWEPT_FACE",FACE,{"disambiguationData":[OSD([subQ1])]})})]});}
            var Q2;
            Q2=makeQuery(id+"F9.opFillet","BLEND_EDGE",EDGE,{"blendedFrom":[makeQuery(id+"F2.opExtrude","CAP_EDGE",EDGE,{"disambiguationData":[OSD([sQuery(id+"F0.wireOp",EDGE,"E7")])],"isStart":false}),makeQuery(id+"F2.opExtrude","SWEPT_FACE",FACE,{"disambiguationData":[OSD([sQuery(id+"F0.wireOp",EDGE,"E19")])]})],"blendedInto":[makeQuery(id+"F2.opExtrude","SWEPT_FACE",FACE,{"disambiguationData":[OSD([sQuery(id+"F0.wireOp",EDGE,"E19")])]})]});
            var Q3;
            {var subQ0=sQuery(id+"F0.wireOp",EDGE,"E6");var subQ1=sQuery(id+"F0.wireOp",EDGE,"E21");Q3=makeQuery(id+"F9.opFillet","BLEND_EDGE",EDGE,{"blendedFrom":[makeQuery(id+"F2.opExtrude","CAP_EDGE",EDGE,{"disambiguationData":[OSD([subQ0])],"isStart":false}),makeQuery(id+"F6.boolean.opBoolean","SPLIT",FACE,{"disambiguationData":[TD([makeQuery(id+"F2.opExtrude","SWEPT_FACE",FACE,{"disambiguationData":[OSD([sQuery(id+"F0.wireOp",EDGE,"E5.rect.right")])]})])],"derivedFrom":makeQuery(id+"F2.opExtrude","SWEPT_FACE",FACE,{"disambiguationData":[OSD([subQ1])]})})],"blendedInto":[makeQuery(id+"F6.boolean.opBoolean","SPLIT",FACE,{"disambiguationData":[TD([makeQuery(id+"F2.opExtrude","SWEPT_FACE",FACE,{"disambiguationData":[OSD([sQuery(id+"F0.wireOp",EDGE,"E5.rect.right")])]})])],"derivedFrom":makeQuery(id+"F2.opExtrude","SWEPT_FACE",FACE,{"disambiguationData":[OSD([subQ1])]})})]});}
            fillet(context, id + "F13", {"entities" : qUnion([Q0, Q1, Q2, Q3]), "radius" : 1 * mm, "tangentPropagation" : true, "allowEdgeOverflow" : false});
        }
        {
            var Q0;
            Q0=makeQuery(id+"F6.boolean.opBoolean","INTERSECT",EDGE,{"derivedFrom":[makeQuery(id+"F2.opExtrude","SWEPT_FACE",FACE,{"disambiguationData":[OSD([sQuery(id+"F0.wireOp",EDGE,"E18")])]}),makeQuery(id+"F6.opExtrude","SWEPT_FACE",FACE,{"disambiguationData":[OSD([sQuery(id+"F4.wireOp",EDGE,"E33")])]})]});
            var Q1;
            Q1=makeQuery(id+"F6.boolean.opBoolean","INTERSECT",EDGE,{"derivedFrom":[makeQuery(id+"F2.opExtrude","SWEPT_FACE",FACE,{"disambiguationData":[OSD([sQuery(id+"F0.wireOp",EDGE,"E19")])]}),makeQuery(id+"F6.opExtrude","SWEPT_FACE",FACE,{"disambiguationData":[OSD([sQuery(id+"F4.wireOp",EDGE,"E32")])]})]});
            var Q2;
            Q2=makeQuery(id+"F6.boolean.opBoolean","INTERSECT",EDGE,{"derivedFrom":[makeQuery(id+"F2.opExtrude","SWEPT_FACE",FACE,{"disambiguationData":[OSD([sQuery(id+"F0.wireOp",EDGE,"E20")])]}),makeQuery(id+"F6.opExtrude","SWEPT_FACE",FACE,{"disambiguationData":[OSD([sQuery(id+"F4.wireOp",EDGE,"E33")])]})]});
            var Q3;
            Q3=makeQuery(id+"F6.boolean.opBoolean","INTERSECT",EDGE,{"derivedFrom":[makeQuery(id+"F2.opExtrude","SWEPT_FACE",FACE,{"disambiguationData":[OSD([sQuery(id+"F0.wireOp",EDGE,"E21")])]}),makeQuery(id+"F6.opExtrude","SWEPT_FACE",FACE,{"disambiguationData":[OSD([sQuery(id+"F4.wireOp",EDGE,"E32")])]})]});
            fillet(context, id + "F14", {"entities" : qUnion([Q0, Q1, Q2, Q3]), "radius" : 5 * mm, "tangentPropagation" : true, "allowEdgeOverflow" : false});
        }
        {
            var Q0;
            {var subQ0=sQuery(id+"F4.wireOp",EDGE,"E33");Q0=makeQuery(id+"F14.opFillet","BLEND_EDGE",EDGE,{"blendedFrom":[makeQuery(id+"F6.boolean.opBoolean","INTERSECT",EDGE,{"derivedFrom":[makeQuery(id+"F2.opExtrude","SWEPT_FACE",FACE,{"disambiguationData":[OSD([sQuery(id+"F0.wireOp",EDGE,"E20")])]}),makeQuery(id+"F6.opExtrude","SWEPT_FACE",FACE,{"disambiguationData":[OSD([subQ0])]})]}),makeQuery(id+"F6.opExtrude","CAP_FACE",FACE,{"disambiguationData":[OSD([sQuery(id+"F4.wireOp",EDGE,"E31"),subQ0])],"isStart":false})],"blendedInto":[makeQuery(id+"F6.opExtrude","CAP_FACE",FACE,{"disambiguationData":[OSD([sQuery(id+"F4.wireOp",EDGE,"E31"),subQ0])],"isStart":false})]});}
            var Q1;
            {var subQ0=sQuery(id+"F4.wireOp",EDGE,"E32");Q1=makeQuery(id+"F14.opFillet","BLEND_EDGE",EDGE,{"blendedFrom":[makeQuery(id+"F6.boolean.opBoolean","INTERSECT",EDGE,{"derivedFrom":[makeQuery(id+"F2.opExtrude","SWEPT_FACE",FACE,{"disambiguationData":[OSD([sQuery(id+"F0.wireOp",EDGE,"E21")])]}),makeQuery(id+"F6.opExtrude","SWEPT_FACE",FACE,{"disambiguationData":[OSD([subQ0])]})]}),makeQuery(id+"F6.opExtrude","CAP_FACE",FACE,{"disambiguationData":[OSD([sQuery(id+"F4.wireOp",EDGE,"E30"),subQ0])],"isStart":false})],"blendedInto":[makeQuery(id+"F6.opExtrude","CAP_FACE",FACE,{"disambiguationData":[OSD([sQuery(id+"F4.wireOp",EDGE,"E30"),subQ0])],"isStart":false})]});}
            var Q2;
            {var subQ0=sQuery(id+"F4.wireOp",EDGE,"E33");Q2=makeQuery(id+"F14.opFillet","BLEND_EDGE",EDGE,{"blendedFrom":[makeQuery(id+"F6.boolean.opBoolean","INTERSECT",EDGE,{"derivedFrom":[makeQuery(id+"F2.opExtrude","SWEPT_FACE",FACE,{"disambiguationData":[OSD([sQuery(id+"F0.wireOp",EDGE,"E18")])]}),makeQuery(id+"F6.opExtrude","SWEPT_FACE",FACE,{"disambiguationData":[OSD([subQ0])]})]}),makeQuery(id+"F6.opExtrude","CAP_FACE",FACE,{"disambiguationData":[OSD([sQuery(id+"F4.wireOp",EDGE,"E31"),subQ0])],"isStart":true})],"blendedInto":[makeQuery(id+"F6.opExtrude","CAP_FACE",FACE,{"disambiguationData":[OSD([sQuery(id+"F4.wireOp",EDGE,"E31"),subQ0])],"isStart":true})]});}
            var Q3;
            {var subQ0=sQuery(id+"F4.wireOp",EDGE,"E32");Q3=makeQuery(id+"F14.opFillet","BLEND_EDGE",EDGE,{"blendedFrom":[makeQuery(id+"F6.boolean.opBoolean","INTERSECT",EDGE,{"derivedFrom":[makeQuery(id+"F2.opExtrude","SWEPT_FACE",FACE,{"disambiguationData":[OSD([sQuery(id+"F0.wireOp",EDGE,"E19")])]}),makeQuery(id+"F6.opExtrude","SWEPT_FACE",FACE,{"disambiguationData":[OSD([subQ0])]})]}),makeQuery(id+"F6.opExtrude","CAP_FACE",FACE,{"disambiguationData":[OSD([sQuery(id+"F4.wireOp",EDGE,"E30"),subQ0])],"isStart":true})],"blendedInto":[makeQuery(id+"F6.opExtrude","CAP_FACE",FACE,{"disambiguationData":[OSD([sQuery(id+"F4.wireOp",EDGE,"E30"),subQ0])],"isStart":true})]});}
            fillet(context, id + "F15", {"entities" : qUnion([Q0, Q1, Q2, Q3]), "radius" : 1 * mm, "tangentPropagation" : true, "allowEdgeOverflow" : false});
        }
        {
            var Q0;
            Q0=makeQuery(id+"F6.opExtrude","CAP_EDGE",EDGE,{"disambiguationData":[OSD([sQuery(id+"F4.wireOp",EDGE,"E31")])],"isStart":false});
            var Q1;
            Q1=makeQuery(id+"F6.opExtrude","CAP_EDGE",EDGE,{"disambiguationData":[OSD([sQuery(id+"F4.wireOp",EDGE,"E30")])],"isStart":false});
            var Q2;
            {var subQ0=sQuery(id+"F0.wireOp",EDGE,"E0.rect.top");var subQ3=sQuery(id+"F0.wireOp",EDGE,"E0.rect.right");var subQ4=sQuery(id+"F0.wireOp",EDGE,"E6");var subQ5=makeQuery(id+"F2.opExtrude","SWEPT_FACE",FACE,{"disambiguationData":[OSD([subQ0]),TDD([makeQuery(id+"F0.imprint","IMPRINT",EDGE,{"disambiguationData":[TD([[makeQuery(id+"F0.imprint","INTERSECT",VERTEX,{"derivedFrom":[subQ0,subQ3,subQ4]}),1.0]])],"derivedFrom":subQ0})])]});var subQ6=sQuery(id+"F4.wireOp",EDGE,"E30");var subQ7=sQuery(id+"F4.wireOp",EDGE,"E32");Q2=makeQuery(id+"F5.boolean.opBoolean","INTERSECT",EDGE,{"derivedFrom":[makeQuery(id+"F7.boolean.opBoolean","MERGE",FACE,{"derivedFrom":[makeQuery(id+"F6.boolean.opBoolean","SPLIT",FACE,{"disambiguationData":[TD([makeQuery(id+"F6.opExtrude","SWEPT_FACE",FACE,{"disambiguationData":[OSD([subQ6])]})])],"derivedFrom":subQ5}),makeQuery(id+"F6.boolean.opBoolean","SPLIT",FACE,{"disambiguationData":[TD([makeQuery(id+"F2.opExtrude","SWEPT_FACE",FACE,{"disambiguationData":[OSD([sQuery(id+"F0.wireOp",EDGE,"E5.rect.right")])]})])],"derivedFrom":subQ5}),makeQuery(id+"F7.opExtrude","CAP_FACE",FACE,{"disambiguationData":[OSD([subQ6,subQ7])],"isStart":true})]}),makeQuery(id+"F5.opExtrude","SWEPT_FACE",FACE,{"disambiguationData":[OSD([subQ6])]})]});}
            var Q3;
            {var subQ0=sQuery(id+"F0.wireOp",EDGE,"E0.rect.top");var subQ3=sQuery(id+"F0.wireOp",EDGE,"E0.rect.left");var subQ4=sQuery(id+"F0.wireOp",EDGE,"E4");var subQ5=makeQuery(id+"F2.opExtrude","SWEPT_FACE",FACE,{"disambiguationData":[OSD([subQ0]),TDD([makeQuery(id+"F0.imprint","IMPRINT",EDGE,{"disambiguationData":[TD([[makeQuery(id+"F0.imprint","INTERSECT",VERTEX,{"derivedFrom":[subQ0,subQ3,subQ4]}),-1.0]])],"derivedFrom":subQ0})])]});var subQ6=sQuery(id+"F4.wireOp",EDGE,"E31");var subQ7=sQuery(id+"F4.wireOp",EDGE,"E33");var subQ8=sQuery(id+"F0.wireOp",EDGE,"E3");Q3=makeQuery(id+"F5.boolean.opBoolean","INTERSECT",EDGE,{"derivedFrom":[makeQuery(id+"F7.boolean.opBoolean","MERGE",FACE,{"derivedFrom":[makeQuery(id+"F6.boolean.opBoolean","SPLIT",FACE,{"disambiguationData":[TD([makeQuery(id+"F6.opExtrude","SWEPT_FACE",FACE,{"disambiguationData":[OSD([subQ6])]})])],"derivedFrom":subQ5}),makeQuery(id+"F6.boolean.opBoolean","SPLIT",FACE,{"disambiguationData":[TD([makeQuery(id+"F2.opExtrude","SWEPT_FACE",FACE,{"disambiguationData":[OSD([subQ8])]})])],"derivedFrom":subQ5}),makeQuery(id+"F7.opExtrude","CAP_FACE",FACE,{"disambiguationData":[OSD([subQ6,subQ7])],"isStart":true})]}),makeQuery(id+"F5.opExtrude","SWEPT_FACE",FACE,{"disambiguationData":[OSD([subQ6])]})]});}
            var Q4;
            {var subQ0=sQuery(id+"F0.wireOp",EDGE,"E0.rect.bottom");var subQ3=sQuery(id+"F0.wireOp",EDGE,"E0.rect.left");var subQ4=sQuery(id+"F0.wireOp",EDGE,"E3");var subQ5=makeQuery(id+"F2.opExtrude","SWEPT_FACE",FACE,{"disambiguationData":[OSD([subQ0]),TDD([makeQuery(id+"F0.imprint","IMPRINT",EDGE,{"disambiguationData":[TD([[makeQuery(id+"F0.imprint","INTERSECT",VERTEX,{"derivedFrom":[subQ0,subQ3,subQ4]}),-1.0]])],"derivedFrom":subQ0})])]});var subQ6=sQuery(id+"F4.wireOp",EDGE,"E31");var subQ7=sQuery(id+"F4.wireOp",EDGE,"E33");Q4=makeQuery(id+"F5.boolean.opBoolean","INTERSECT",EDGE,{"derivedFrom":[makeQuery(id+"F7.boolean.opBoolean","MERGE",FACE,{"derivedFrom":[makeQuery(id+"F6.boolean.opBoolean","SPLIT",FACE,{"disambiguationData":[TD([makeQuery(id+"F6.opExtrude","SWEPT_FACE",FACE,{"disambiguationData":[OSD([subQ6])]})])],"derivedFrom":subQ5}),makeQuery(id+"F6.boolean.opBoolean","SPLIT",FACE,{"disambiguationData":[TD([makeQuery(id+"F2.opExtrude","SWEPT_FACE",FACE,{"disambiguationData":[OSD([subQ4])]})])],"derivedFrom":subQ5}),makeQuery(id+"F7.opExtrude","CAP_FACE",FACE,{"disambiguationData":[OSD([subQ6,subQ7])],"isStart":false})]}),makeQuery(id+"F5.opExtrude","SWEPT_FACE",FACE,{"disambiguationData":[OSD([subQ6])]})]});}
            var Q5;
            {var subQ0=sQuery(id+"F0.wireOp",EDGE,"E0.rect.bottom");var subQ1=sQuery(id+"F0.wireOp",EDGE,"E5.rect.right");var subQ3=sQuery(id+"F0.wireOp",EDGE,"E0.rect.right");var subQ4=sQuery(id+"F0.wireOp",EDGE,"E7");var subQ5=makeQuery(id+"F2.opExtrude","SWEPT_FACE",FACE,{"disambiguationData":[OSD([subQ0]),TDD([makeQuery(id+"F0.imprint","IMPRINT",EDGE,{"disambiguationData":[TD([[makeQuery(id+"F0.imprint","INTERSECT",VERTEX,{"derivedFrom":[subQ0,subQ3,subQ4]}),1.0]])],"derivedFrom":subQ0})])]});var subQ6=sQuery(id+"F4.wireOp",EDGE,"E30");var subQ7=sQuery(id+"F4.wireOp",EDGE,"E32");Q5=makeQuery(id+"F5.boolean.opBoolean","INTERSECT",EDGE,{"derivedFrom":[makeQuery(id+"F7.boolean.opBoolean","MERGE",FACE,{"derivedFrom":[makeQuery(id+"F6.boolean.opBoolean","SPLIT",FACE,{"disambiguationData":[TD([makeQuery(id+"F6.opExtrude","SWEPT_FACE",FACE,{"disambiguationData":[OSD([subQ6])]})])],"derivedFrom":subQ5}),makeQuery(id+"F6.boolean.opBoolean","SPLIT",FACE,{"disambiguationData":[TD([makeQuery(id+"F2.opExtrude","SWEPT_FACE",FACE,{"disambiguationData":[OSD([subQ1])]})])],"derivedFrom":subQ5}),makeQuery(id+"F7.opExtrude","CAP_FACE",FACE,{"disambiguationData":[OSD([subQ6,subQ7])],"isStart":false})]}),makeQuery(id+"F5.opExtrude","SWEPT_FACE",FACE,{"disambiguationData":[OSD([subQ6])]})]});}
            fillet(context, id + "F16", {"entities" : qUnion([Q0, Q1, Q2, Q3, Q4, Q5]), "radius" : 0.5 * mm, "tangentPropagation" : true, "allowEdgeOverflow" : false});
        }
        {
            var Q0;
            Q0=makeQuery(id+"F8.boolean.opBoolean","COPY",FACE,{"disambiguationData":[OD(1.0)],"derivedFrom":makeQuery(id+"F8.opExtrude","SWEPT_FACE",FACE,{"disambiguationData":[OSD([sQuery(id+"F4.wireOp",EDGE,"E35")])]})});
            var Q1;
            Q1=makeQuery(id+"F8.boolean.opBoolean","COPY",FACE,{"disambiguationData":[OD(1.0)],"derivedFrom":makeQuery(id+"F8.opExtrude","SWEPT_FACE",FACE,{"disambiguationData":[OSD([sQuery(id+"F4.wireOp",EDGE,"E34")])]})});
            var Q2;
            Q2=makeQuery(id+"F8.boolean.opBoolean","COPY",FACE,{"disambiguationData":[OD(0.0)],"derivedFrom":makeQuery(id+"F8.opExtrude","SWEPT_FACE",FACE,{"disambiguationData":[OSD([sQuery(id+"F4.wireOp",EDGE,"E34")])]})});
            var Q3;
            Q3=makeQuery(id+"F8.boolean.opBoolean","COPY",FACE,{"disambiguationData":[OD(0.0)],"derivedFrom":makeQuery(id+"F8.opExtrude","SWEPT_FACE",FACE,{"disambiguationData":[OSD([sQuery(id+"F4.wireOp",EDGE,"E35")])]})});
            fillet(context, id + "F17", {"entities" : qUnion([Q0, Q1, Q2, Q3]), "radius" : 2 * mm, "tangentPropagation" : true, "allowEdgeOverflow" : false});
        }
    });
